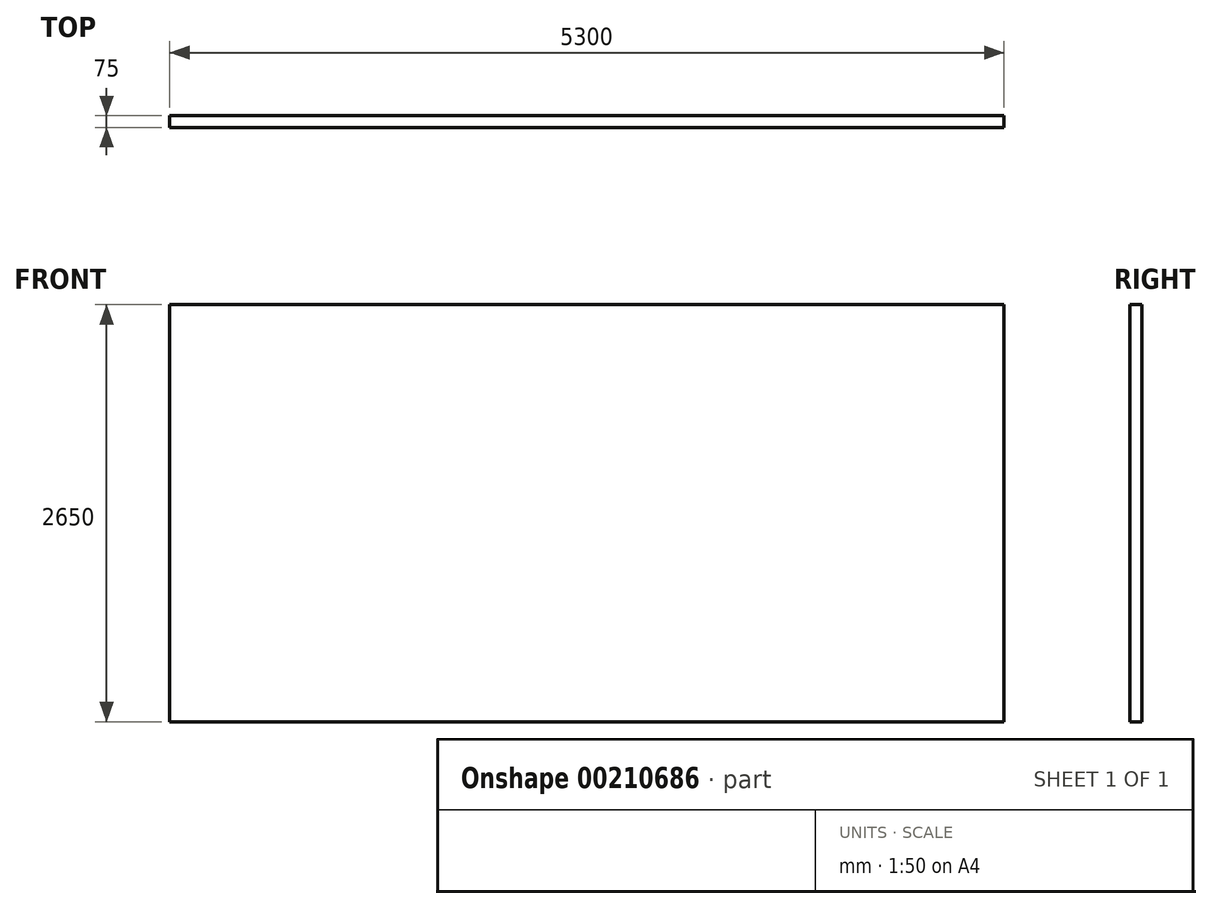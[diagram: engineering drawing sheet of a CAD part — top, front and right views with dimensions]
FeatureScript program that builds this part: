
annotation { "Feature Type Name" : "Feature", "Feature Type Description" : "" }
export const myFeature = defineFeature(function(context is Context, id is Id, definition is map)
    precondition{}
    {
        {
            var Q0;
            Q0=qCreatedBy(makeId("Front.planeOp"),FACE);
            var sketch = newSketch(context, id + "F0", { "sketchPlane" : qUnion([Q0])});
            skLineSegment(sketch, "E0.bottom", {"start": v(0, 0) * mm, "end": v(5300, 0) * mm});
            skLineSegment(sketch, "E0.left", {"start": v(0, 0) * mm, "end": v(0, 2650) * mm});
            skLineSegment(sketch, "E0.right", {"start": v(5300, 0) * mm, "end": v(5300, 2650) * mm});
            skLineSegment(sketch, "E1", {"start": v(0, 2650) * mm, "end": v(5300, 2650) * mm});
            skSolve(sketch);
        }
        {
            var Q0;
            Q0=makeQuery(id+"F0.imprint","IMPRINT",FACE,{"disambiguationData":[TD([[makeQuery(id+"F0.imprint","IMPRINT",EDGE,{"derivedFrom":sQuery(id+"F0.wireOp",EDGE,"E0.bottom")}),1.0]])]});
            extrude(context, id + "F1", {"entities" : qUnion([Q0]), "depth" : 75 * mm});
        }
    });
